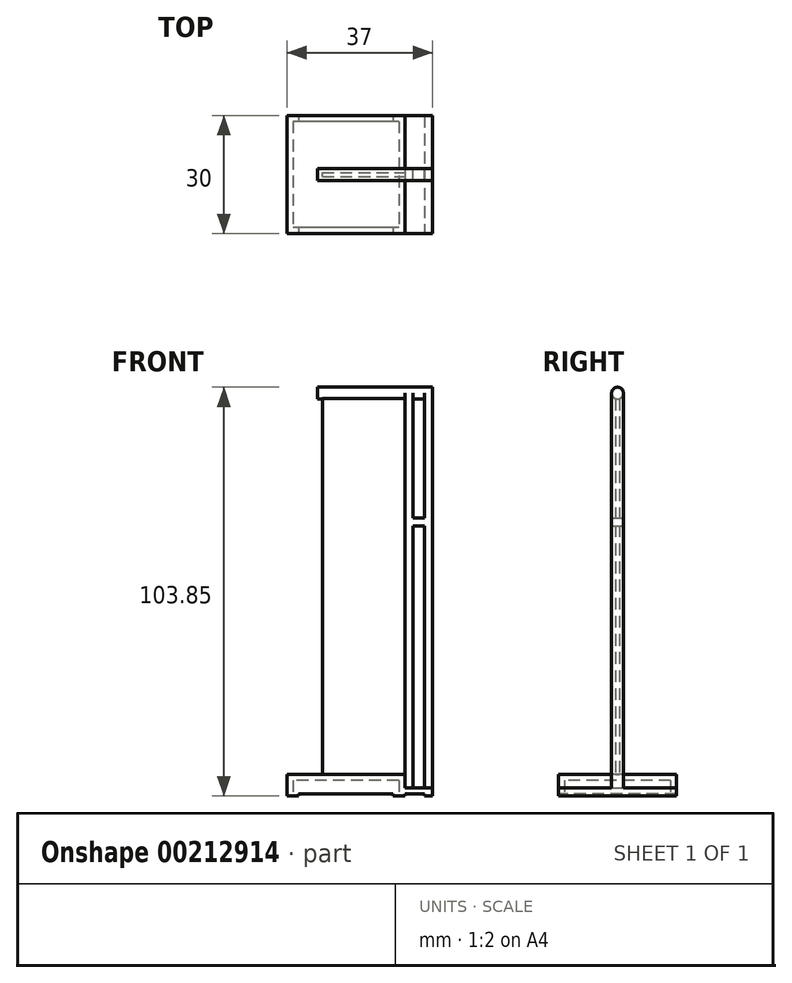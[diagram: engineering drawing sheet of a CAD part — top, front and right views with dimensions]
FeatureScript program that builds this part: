
annotation { "Feature Type Name" : "Feature", "Feature Type Description" : "" }
export const myFeature = defineFeature(function(context is Context, id is Id, definition is map)
    precondition{}
    {
        {
            var Q0;
            Q0=qCreatedBy(makeId("Top.planeOp"),FACE);
            var sketch = newSketch(context, id + "F0", { "sketchPlane" : qUnion([Q0])});
            skLineSegment(sketch, "E0.bottom", {"start": v(15, 15) * mm, "end": v(-15, 15) * mm});
            skLineSegment(sketch, "E0.top", {"start": v(15, -15) * mm, "end": v(-15, -15) * mm});
            skLineSegment(sketch, "E0.left", {"start": v(15, 15) * mm, "end": v(15, -15) * mm});
            skLineSegment(sketch, "E0.right", {"start": v(-15, 15) * mm, "end": v(-15, -15) * mm});
            skPoint(sketch, "E0.middle", {"position": v(0, 0) * mm});
            skSolve(sketch);
        }
        {
            var Q0;
            Q0=makeQuery(id+"F0.imprint","IMPRINT",FACE,{"disambiguationData":[TD([[makeQuery(id+"F0.imprint","IMPRINT",EDGE,{"derivedFrom":sQuery(id+"F0.wireOp",EDGE,"E0.bottom")}),1.0]])]});
            extrude(context, id + "F1", {"entities" : qUnion([Q0]), "depth" : (110 / 20) * mm});
        }
        {
            var Q0;
            Q0=makeQuery(id+"F1.opExtrude","CAP_FACE",FACE,{"disambiguationData":[OSD([sQuery(id+"F0.wireOp",EDGE,"E0.bottom"),sQuery(id+"F0.wireOp",EDGE,"E0.top"),sQuery(id+"F0.wireOp",EDGE,"E0.left"),sQuery(id+"F0.wireOp",EDGE,"E0.right")])],"isStart":true});
            shell(context, id + "F2", {"entities" : qUnion([Q0]), "thickness" : 1.5 * mm});
        }
        {
            var Q0;
            Q0=qCreatedBy(makeId("Front.planeOp"),FACE);
            var sketch = newSketch(context, id + "F3", { "sketchPlane" : qUnion([Q0])});
            skLineSegment(sketch, "E1.0", {"start": v(15, 5.5) * mm, "end": v(15, 0) * mm, "construction": true});
            skLineSegment(sketch, "E2", {"start": v(15, 0) * mm, "end": v(15, 102.35) * mm});
            skLineSegment(sketch, "E3", {"start": v(22, 102.35) * mm, "end": v(22, 0) * mm});
            skLineSegment(sketch, "E4", {"start": v(22, 0) * mm, "end": v(20, 0) * mm});
            skLineSegment(sketch, "E5", {"start": v(20, 0) * mm, "end": v(20, 102.35) * mm});
            skLineSegment(sketch, "E6", {"start": v(17, 102.35) * mm, "end": v(17, 0) * mm});
            skLineSegment(sketch, "E7", {"start": v(17, 0) * mm, "end": v(15, 0) * mm});
            skLineSegment(sketch, "E8", {"start": v(15, 102.35) * mm, "end": v(17, 102.35) * mm});
            skLineSegment(sketch, "E9", {"start": v(20, 102.35) * mm, "end": v(22, 102.35) * mm});
            skSolve(sketch);
        }
        {
            var Q0;
            Q0=qSketchRegion(id+"F3",true);
            extrude(context, id + "F4", {"entities" : qUnion([Q0]), "operationType" : NewBodyOperationType.ADD, "endBound" : BoundingType.SYMMETRIC, "depth" : 3 * mm});
        }
        {
            var Q0;
            Q0=makeQuery(id+"F4.opExtrude","SWEPT_FACE",FACE,{"disambiguationData":[OSD([sQuery(id+"F3.wireOp",EDGE,"E3")])]});
            var sketch = newSketch(context, id + "F5", { "sketchPlane" : qUnion([Q0])});
            skCircle(sketch, "E10", {"center": v(0, 102.35) * mm, "radius": 1.5 * mm});
            skSolve(sketch);
        }
        {
            var Q0;
            {var subQ1=sQuery(id+"F3.wireOp",EDGE,"E3");var subQ2=makeQuery(id+"F4.opExtrude","SWEPT_EDGE",EDGE,{"disambiguationData":[OSD([subQ1,sQuery(id+"F3.wireOp",EDGE,"E9")])]});Q0=makeQuery(id+"F5.imprint","IMPRINT",FACE,{"disambiguationData":[TD([[makeQuery(id+"F5.imprint","IMPRINT",EDGE,{"derivedFrom":subQ2}),1.0]])]});}
            var Q1;
            {var subQ1=sQuery(id+"F3.wireOp",EDGE,"E3");var subQ2=makeQuery(id+"F4.opExtrude","SWEPT_EDGE",EDGE,{"disambiguationData":[OSD([subQ1,sQuery(id+"F3.wireOp",EDGE,"E9")])]});Q1=makeQuery(id+"F5.imprint","IMPRINT",FACE,{"disambiguationData":[TD([[makeQuery(id+"F5.imprint","IMPRINT",EDGE,{"derivedFrom":subQ2}),-1.0]])]});}
            extrude(context, id + "F6", {"entities" : qUnion([Q0, Q1]), "operationType" : NewBodyOperationType.ADD, "oppositeDirection" : true, "depth" : (585 / 20) * mm});
        }
        {
            var Q0;
            Q0=qCreatedBy(makeId("Top.planeOp"),FACE);
            var sketch = newSketch(context, id + "F7", { "sketchPlane" : qUnion([Q0])});
            skLineSegment(sketch, "E11.bottom", {"start": v(15, -15) * mm, "end": v(22, -15) * mm});
            skLineSegment(sketch, "E11.top", {"start": v(15, 15) * mm, "end": v(22, 15) * mm});
            skLineSegment(sketch, "E11.left", {"start": v(15, -15) * mm, "end": v(15, 15) * mm});
            skLineSegment(sketch, "E11.right", {"start": v(22, -15) * mm, "end": v(22, 15) * mm});
            skSolve(sketch);
        }
        {
            var Q0;
            Q0=makeQuery(id+"F7.imprint","IMPRINT",FACE,{"disambiguationData":[TD([[makeQuery(id+"F7.imprint","IMPRINT",EDGE,{"derivedFrom":sQuery(id+"F7.wireOp",EDGE,"E11.bottom")}),1.0]])]});
            extrude(context, id + "F8", {"entities" : qUnion([Q0]), "operationType" : NewBodyOperationType.ADD, "depth" : 2 * mm});
        }
        {
            var Q0;
            Q0=makeQuery(id+"F1.opExtrude","CAP_VERTEX",VERTEX,{"disambiguationData":[OSD([sQuery(id+"F0.wireOp",EDGE,"E0.top"),sQuery(id+"F0.wireOp",EDGE,"E0.left")])],"isStart":false});
            var Q1;
            Q1=makeQuery(id+"F1.opExtrude","CAP_VERTEX",VERTEX,{"disambiguationData":[OSD([sQuery(id+"F0.wireOp",EDGE,"E0.bottom"),sQuery(id+"F0.wireOp",EDGE,"E0.right")])],"isStart":false});
            var Q2;
            Q2=makeQuery(id+"F1.opExtrude","CAP_VERTEX",VERTEX,{"disambiguationData":[OSD([sQuery(id+"F0.wireOp",EDGE,"E0.bottom"),sQuery(id+"F0.wireOp",EDGE,"E0.right")])],"isStart":true});
            cPlane(context, id + "F9", {"entities" : qUnion([Q0, Q1, Q2]), "cplaneType" : CPlaneType.THREE_POINT, "offset" : 25 * mm, "width" : 150 * mm, "height" : 150 * mm});
        }
        {
            var Q0;
            Q0=qCreatedBy(makeId("Front.planeOp"),FACE);
            var sketch = newSketch(context, id + "F10", { "sketchPlane" : qUnion([Q0])});
            skLineSegment(sketch, "E12.bottom", {"start": v(12, 0) * mm, "end": v(-12, 0) * mm});
            skLineSegment(sketch, "E12.top", {"start": v(12, 0.5) * mm, "end": v(-12, 0.5) * mm});
            skLineSegment(sketch, "E12.left", {"start": v(12, 0) * mm, "end": v(12, 0.5) * mm});
            skLineSegment(sketch, "E12.right", {"start": v(-12, 0) * mm, "end": v(-12, 0.5) * mm});
            skPoint(sketch, "E12.middle", {"position": v(0, 0.25) * mm});
            skLineSegment(sketch, "E13.bottom", {"start": v(15, 0) * mm, "end": v(20, 0) * mm});
            skLineSegment(sketch, "E13.top", {"start": v(15, 0.5) * mm, "end": v(20, 0.5) * mm});
            skLineSegment(sketch, "E13.left", {"start": v(15, 0) * mm, "end": v(15, 0.5) * mm});
            skLineSegment(sketch, "E13.right", {"start": v(20, 0) * mm, "end": v(20, 0.5) * mm});
            skSolve(sketch);
        }
        {
            var Q0;
            Q0=qSketchRegion(id+"F10",true);
            extrude(context, id + "F11", {"entities" : qUnion([Q0]), "operationType" : NewBodyOperationType.REMOVE, "endBound" : BoundingType.SYMMETRIC, "oppositeDirection" : true, "depth" : 50 * mm});
        }
        {
            var Q0;
            Q0=qCreatedBy(makeId("Front.planeOp"),FACE);
            var sketch = newSketch(context, id + "F12", { "sketchPlane" : qUnion([Q0])});
            skLineSegment(sketch, "E14.bottom", {"start": v(20, 70.6) * mm, "end": v(17, 70.6) * mm});
            skLineSegment(sketch, "E14.top", {"start": v(20, 68.6) * mm, "end": v(17, 68.6) * mm});
            skLineSegment(sketch, "E14.left", {"start": v(20, 70.6) * mm, "end": v(20, 68.6) * mm});
            skLineSegment(sketch, "E14.right", {"start": v(17, 70.6) * mm, "end": v(17, 68.6) * mm});
            skSolve(sketch);
        }
        {
            var Q0;
            Q0=makeQuery(id+"F12.imprint","IMPRINT",FACE,{"disambiguationData":[TD([[makeQuery(id+"F12.imprint","IMPRINT",EDGE,{"derivedFrom":sQuery(id+"F12.wireOp",EDGE,"E14.bottom")}),1.0]])]});
            var Q1;
            Q1=makeQuery(id+"F4.opExtrude","CAP_FACE",FACE,{"disambiguationData":[OSD([sQuery(id+"F3.wireOp",EDGE,"E3"),sQuery(id+"F3.wireOp",EDGE,"E4"),sQuery(id+"F3.wireOp",EDGE,"E5"),sQuery(id+"F3.wireOp",EDGE,"E9")])],"isStart":false});
            var Q2;
            Q2=makeQuery(id+"F4.opExtrude","CAP_FACE",FACE,{"disambiguationData":[OSD([sQuery(id+"F3.wireOp",EDGE,"E3"),sQuery(id+"F3.wireOp",EDGE,"E4"),sQuery(id+"F3.wireOp",EDGE,"E5"),sQuery(id+"F3.wireOp",EDGE,"E9")])],"isStart":true});
            extrude(context, id + "F13", {"entities" : qUnion([Q0]), "operationType" : NewBodyOperationType.ADD, "endBound" : BoundingType.UP_TO_SURFACE, "endBoundEntityFace" : qUnion([Q1]), "depth" : 25 * mm, "hasSecondDirection" : true, "secondDirectionBound" : SecondDirectionBoundingType.UP_TO_SURFACE, "secondDirectionOppositeDirection" : true, "secondDirectionBoundEntityFace" : qUnion([Q2]), "secondDirectionDepth" : 25 * mm});
        }
        {
            var Q0;
            Q0=qCreatedBy(makeId("Front.planeOp"),FACE);
            var sketch = newSketch(context, id + "F14", { "sketchPlane" : qUnion([Q0])});
            skLineSegment(sketch, "E15.bottom", {"start": v(-6, 101.35) * mm, "end": v(15, 101.35) * mm});
            skLineSegment(sketch, "E15.top", {"start": v(-6, 5.5) * mm, "end": v(15, 5.5) * mm});
            skLineSegment(sketch, "E15.left", {"start": v(-6, 101.35) * mm, "end": v(-6, 5.5) * mm});
            skLineSegment(sketch, "E15.right", {"start": v(15, 101.35) * mm, "end": v(15, 5.5) * mm});
            skLineSegment(sketch, "E16.0", {"start": v(-7.25, 100.85) * mm, "end": v(-7.25, 103.85) * mm, "construction": true});
            skSolve(sketch);
        }
        {
            var Q0;
            Q0=makeQuery(id+"F14.imprint","IMPRINT",FACE,{"disambiguationData":[TD([[makeQuery(id+"F14.imprint","IMPRINT",EDGE,{"derivedFrom":sQuery(id+"F14.wireOp",EDGE,"E15.bottom")}),-1.0]])]});
            extrude(context, id + "F15", {"entities" : qUnion([Q0]), "operationType" : NewBodyOperationType.ADD, "endBound" : BoundingType.SYMMETRIC, "depth" : 1 * mm});
        }
    });
